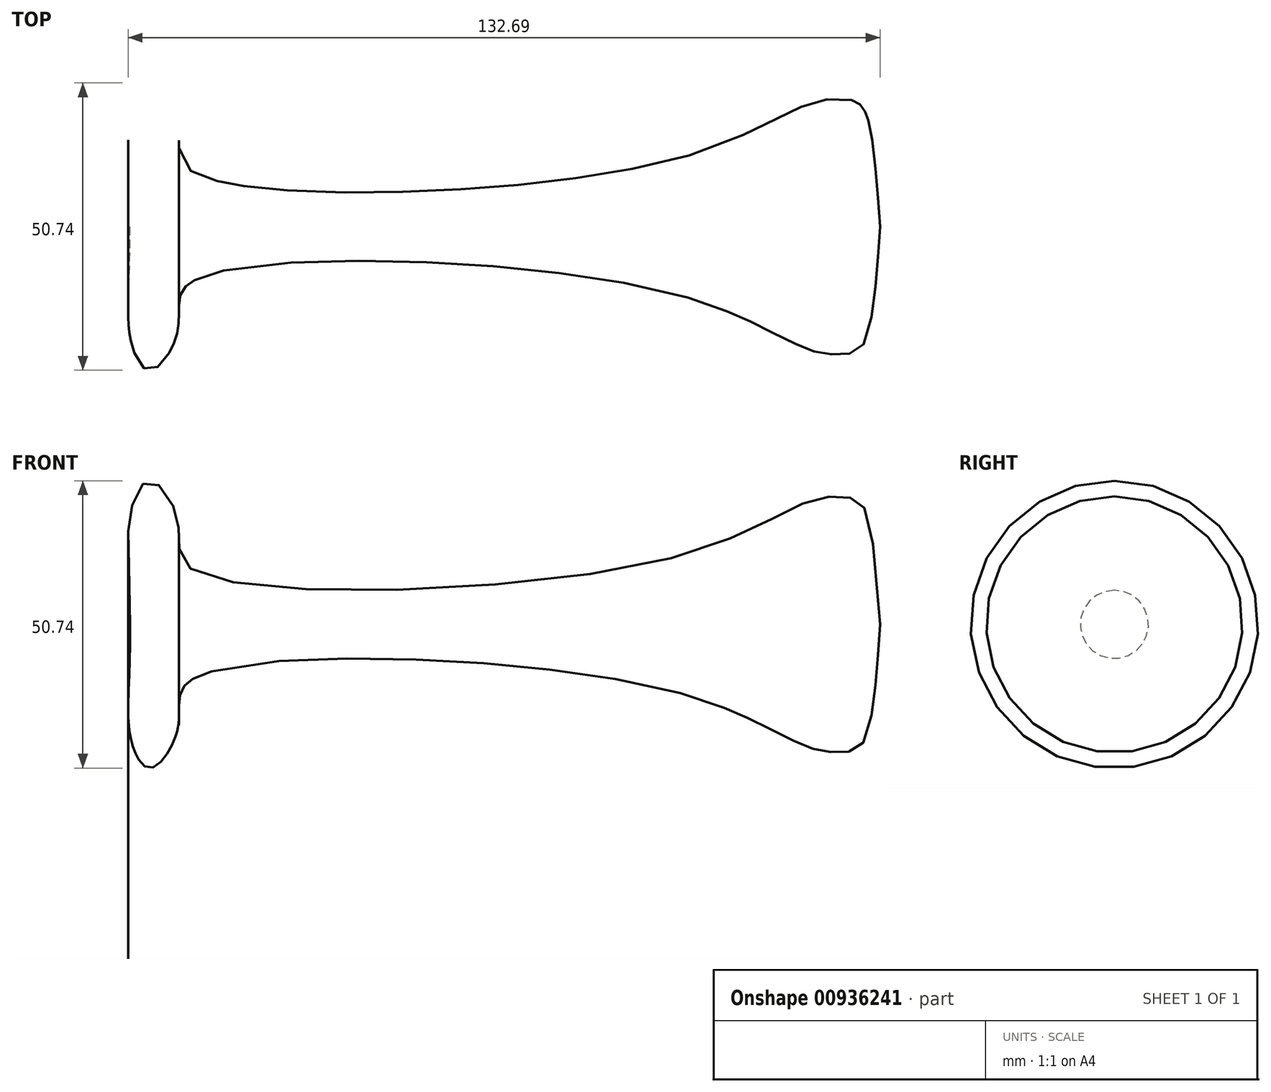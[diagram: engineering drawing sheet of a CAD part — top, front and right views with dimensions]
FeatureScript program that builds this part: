
annotation { "Feature Type Name" : "Feature", "Feature Type Description" : "" }
export const myFeature = defineFeature(function(context is Context, id is Id, definition is map)
    precondition{}
    {
        {
            var Q0;
            Q0=qCreatedBy(makeId("Front.planeOp"),FACE);
            var sketch = newSketch(context, id + "F0", { "sketchPlane" : qUnion([Q0])});
            skFitSpline(sketch, "E0", {"points": [v(-55.64, 0) * mm, v(-55.43, 20.53) * mm, v(-52.27, 25.37) * mm, v(-48.06, 20.95) * mm, v(-47, 15.05) * mm, v(-44.48, 9.54) * mm, v(38.9, 11.48) * mm, v(64.37, 21.8) * mm, v(71.32, 22.42) * mm, v(76.71, 0) * mm], "startDerivative": vector(0, 297.7) * mm, "endDerivative": vector(28.95, -444.82) * mm});
            skLineSegment(sketch, "E1", {"start": v(-55.64, 0) * mm, "end": v(76.71, 0) * mm});
            skSolve(sketch);
        }
        {
            var Q0;
            Q0=makeQuery(id+"F0.imprint","IMPRINT",FACE,{"disambiguationData":[TD([[makeQuery(id+"F0.imprint","IMPRINT",EDGE,{"derivedFrom":sQuery(id+"F0.wireOp",EDGE,"E0")}),-1.0]])]});
            var Q1;
            Q1=sQuery(id+"F0.wireOp",EDGE,"E1");
            revolve(context, id + "F1", {"surfaceOperationType" : NewSurfaceOperationType.NEW, "entities" : qUnion([Q0]), "axis" : qUnion([Q1]), "revolveType" : RevolveType.FULL});
        }
    });
